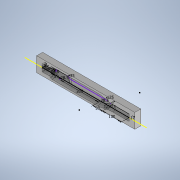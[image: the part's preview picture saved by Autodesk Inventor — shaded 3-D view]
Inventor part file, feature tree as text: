
AUTODESK INVENTOR PART (.ipt)
format: ipt  version: 2022 (Build 260153000, 153)  size: 237,568 bytes
history: native  units: mm
features: sketch x2, extrude x2, revolve x1, fillet x1, boolean_combine x1
ambient origin geometry x8: Origin, YZ Plane, XZ Plane, XY Plane, X Axis, Y Axis, Z Axis, Center Point
bodies: Solid2 (feature_tree), Solid3 (feature_tree)
feature tree (7):
  sketch  "Sketch1"  dims[d0=41.0mm d1=6.0mm]
  revolve  "Revolution2"  [1 undecoded]
  extrude  "Extrusion2"  Depth=200.0mm
  fillet  "Fillet1"  Radius=50.0mm
  extrude  "Extrusion3"  Depth=100.0mm
  boolean_combine  "Combine1"
  sketch  "Sketch2"  dims[d2=59.0mm d3=200.0mm d4=50.0mm d5=100.0mm d6=19.5mm d7=19.5mm d8=28.5mm d10=28.5mm d11=17.0mm d12=17.0mm d13=2.0mm d14=8.0mm d16=125.0mm d17=125.0mm d18=2.0mm d25=35.0mm d26=28.5mm d27=180.0deg d28=100.0mm d29=0.0mm d30=2.0mm d31=516.0mm d32=77.0mm d33=31.5mm d34=0.0mm d19=0.872665mm d20=0.872665mm]
note: 1 required parameter value undecoded (feature->parameter linkage not recoverable at this tier; creation-order binding heuristic only, values carry confidence <= 0.55)
